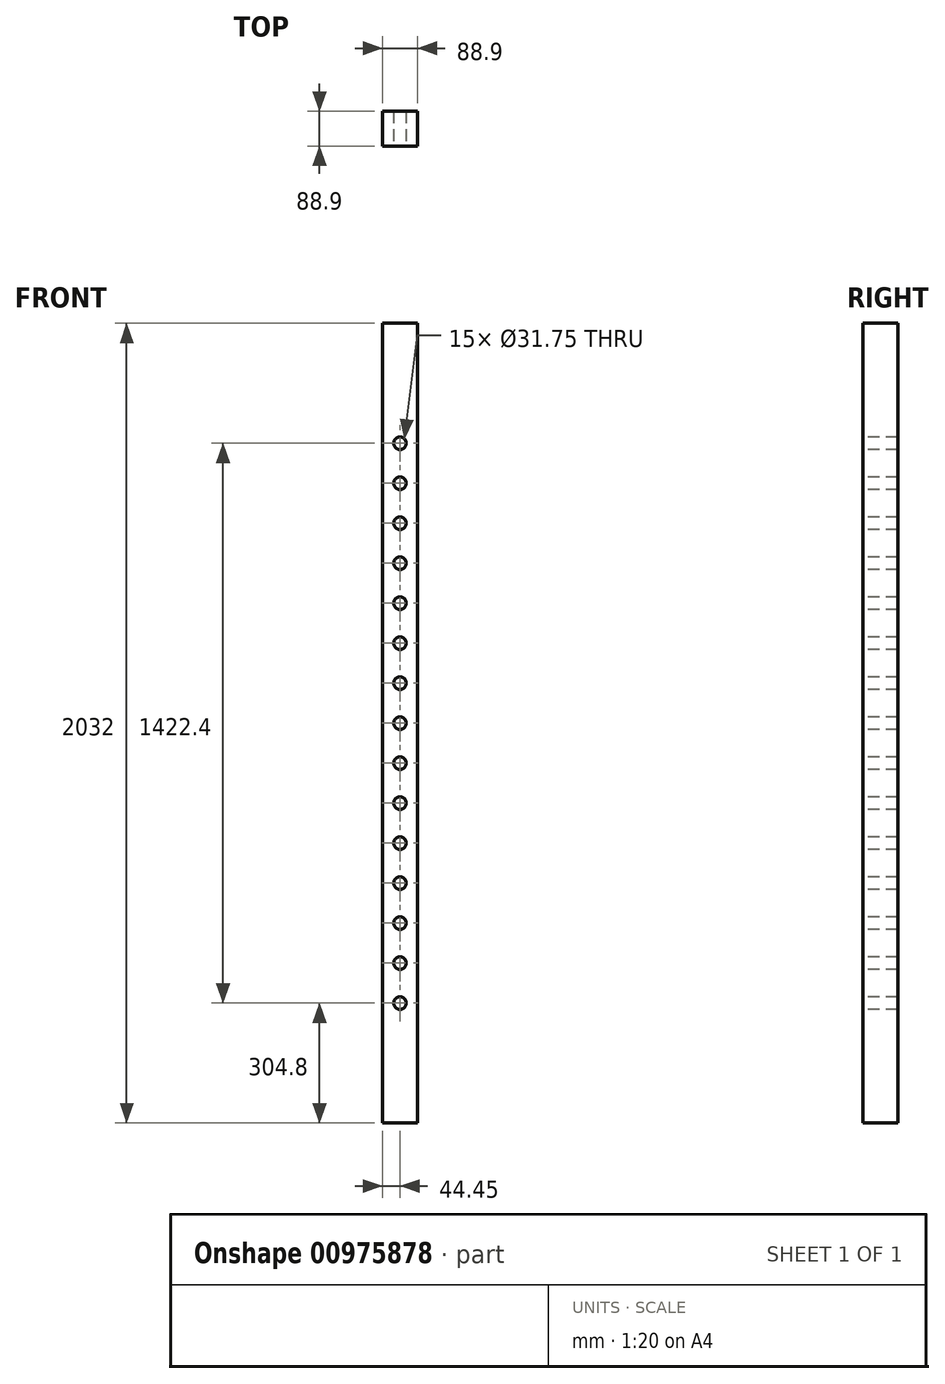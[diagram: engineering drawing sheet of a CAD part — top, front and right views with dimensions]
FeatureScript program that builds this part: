
annotation { "Feature Type Name" : "Feature", "Feature Type Description" : "" }
export const myFeature = defineFeature(function(context is Context, id is Id, definition is map)
    precondition{}
    {
        {
            var Q0;
            Q0=qCreatedBy(makeId("Front.planeOp"),FACE);
            var sketch = newSketch(context, id + "F0", { "sketchPlane" : qUnion([Q0])});
            skLineSegment(sketch, "E0.bottom", {"start": v(44.45, 1016) * mm, "end": v(-44.45, 1016) * mm});
            skLineSegment(sketch, "E0.top", {"start": v(44.45, -1016) * mm, "end": v(-44.45, -1016) * mm});
            skLineSegment(sketch, "E0.left", {"start": v(44.45, 1016) * mm, "end": v(44.45, -1016) * mm});
            skLineSegment(sketch, "E0.right", {"start": v(-44.45, 1016) * mm, "end": v(-44.45, -1016) * mm});
            skPoint(sketch, "E0.middle", {"position": v(0, 0) * mm});
            skCircle(sketch, "E1", {"center": v(0, -711.2) * mm, "radius": 15.88 * mm});
            skCircle(sketch, "E2.0.1.0", {"center": v(0, -609.6) * mm, "radius": 15.88 * mm});
            skCircle(sketch, "E2.0.2.0", {"center": v(0, -508) * mm, "radius": 15.88 * mm});
            skCircle(sketch, "E2.0.3.0", {"center": v(0, -406.4) * mm, "radius": 15.88 * mm});
            skCircle(sketch, "E2.0.4.0", {"center": v(0, -304.8) * mm, "radius": 15.88 * mm});
            skCircle(sketch, "E2.0.5.0", {"center": v(0, -203.2) * mm, "radius": 15.88 * mm});
            skCircle(sketch, "E2.0.6.0", {"center": v(0, -101.6) * mm, "radius": 15.88 * mm});
            skCircle(sketch, "E2.0.7.0", {"center": v(0, 0) * mm, "radius": 15.88 * mm});
            skCircle(sketch, "E2.0.8.0", {"center": v(0, 101.6) * mm, "radius": 15.88 * mm});
            skCircle(sketch, "E2.0.9.0", {"center": v(0, 203.2) * mm, "radius": 15.88 * mm});
            skCircle(sketch, "E2.0.10.0", {"center": v(0, 304.8) * mm, "radius": 15.88 * mm});
            skCircle(sketch, "E2.0.11.0", {"center": v(0, 406.4) * mm, "radius": 15.88 * mm});
            skCircle(sketch, "E2.0.12.0", {"center": v(0, 508) * mm, "radius": 15.88 * mm});
            skCircle(sketch, "E2.0.13.0", {"center": v(0, 609.6) * mm, "radius": 15.88 * mm});
            skLineSegment(sketch, "E2.direction1", {"start": v(0, -711.2) * mm, "end": v(25.4, -711.2) * mm, "construction": true});
            skLineSegment(sketch, "E2.direction2", {"start": v(0, -711.2) * mm, "end": v(0, -609.6) * mm, "construction": true});
            skCircle(sketch, "E3.0.0.14", {"center": v(0, 711.2) * mm, "radius": 15.88 * mm});
            skSolve(sketch);
        }
        {
            var Q0;
            Q0=makeQuery(id+"F0.imprint","IMPRINT",FACE,{"disambiguationData":[TD([[makeQuery(id+"F0.imprint","IMPRINT",EDGE,{"derivedFrom":sQuery(id+"F0.wireOp",EDGE,"E0.bottom")}),1.0]])]});
            extrude(context, id + "F1", {"entities" : qUnion([Q0]), "oppositeDirection" : true, "depth" : 88.9 * mm, "offsetDistance" : 25.4 * mm});
        }
    });
